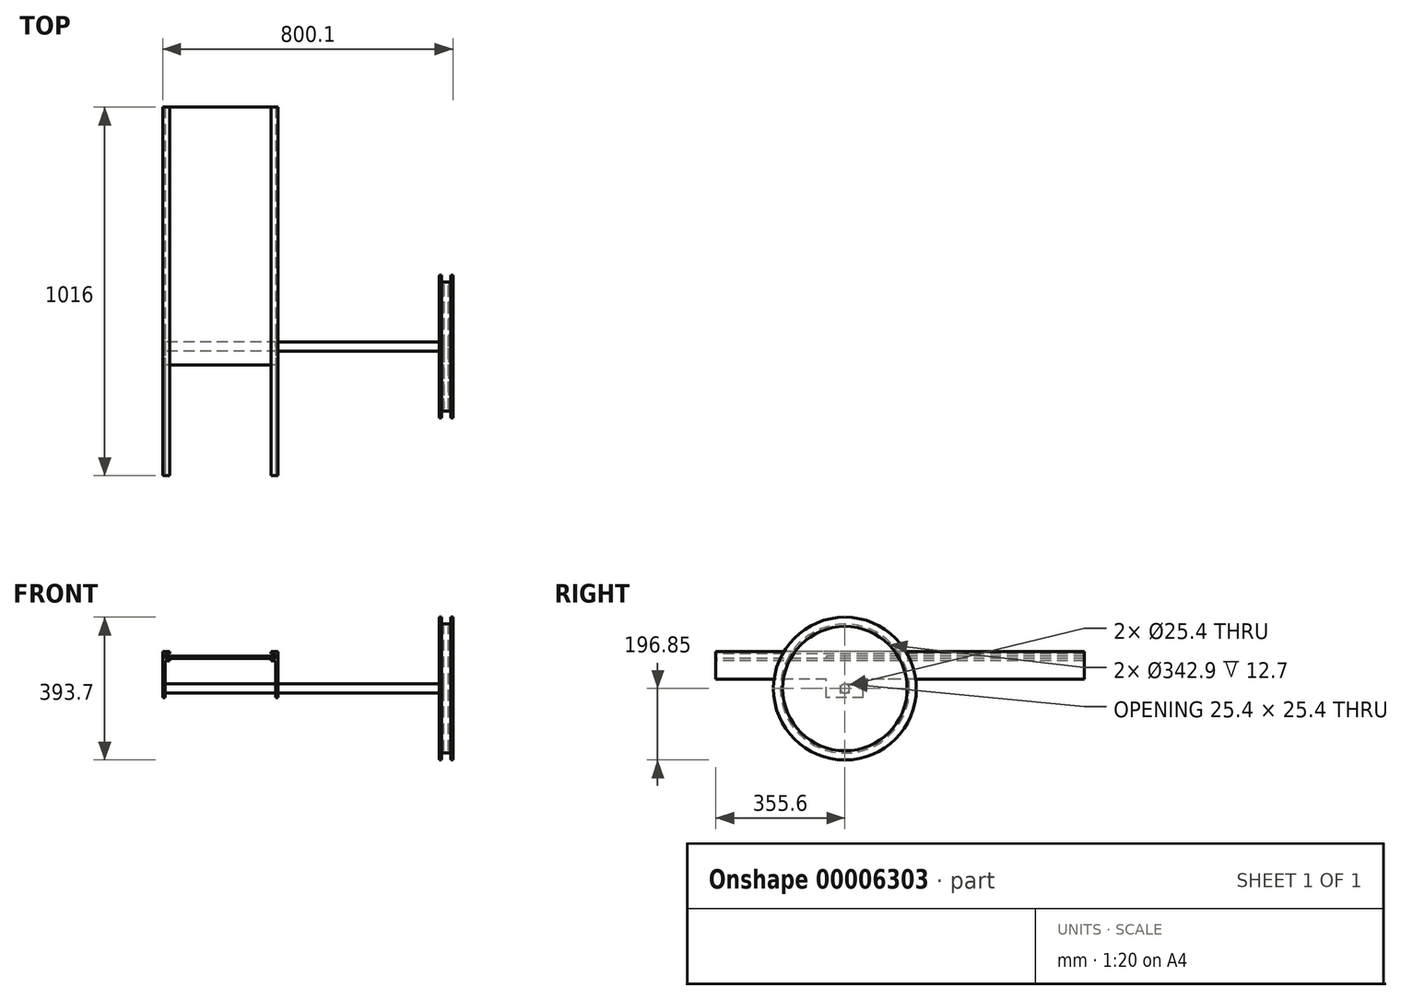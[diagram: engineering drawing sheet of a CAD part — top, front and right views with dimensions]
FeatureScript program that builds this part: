
annotation { "Feature Type Name" : "Feature", "Feature Type Description" : "" }
export const myFeature = defineFeature(function(context is Context, id is Id, definition is map)
    precondition{}
    {
        {
            var Q0;
            Q0=qCreatedBy(makeId("Front.planeOp"),FACE);
            var sketch = newSketch(context, id + "F0", { "sketchPlane" : qUnion([Q0])});
            skLineSegment(sketch, "E0", {"start": v(-158.75, 76.2) * mm, "end": v(-158.75, -50.8) * mm});
            skLineSegment(sketch, "E1", {"start": v(-158.75, -50.8) * mm, "end": v(-152.4, -50.8) * mm});
            skLineSegment(sketch, "E2", {"start": v(-152.4, 50.8) * mm, "end": v(-139.7, 50.8) * mm});
            skLineSegment(sketch, "E3", {"start": v(-139.7, 57.15) * mm, "end": v(-152.4, 57.15) * mm});
            skLineSegment(sketch, "E4", {"start": v(-152.4, 57.15) * mm, "end": v(-152.4, 69.85) * mm});
            skLineSegment(sketch, "E5", {"start": v(-152.4, 69.85) * mm, "end": v(-139.7, 69.85) * mm});
            skLineSegment(sketch, "E6", {"start": v(-139.7, 50.8) * mm, "end": v(-139.7, 57.15) * mm});
            skLineSegment(sketch, "E7", {"start": v(-139.7, 76.2) * mm, "end": v(-158.75, 76.2) * mm});
            skLineSegment(sketch, "E8", {"start": v(-152.4, -50.8) * mm, "end": v(-152.4, 50.8) * mm});
            skLineSegment(sketch, "E9", {"start": v(-152.4, 0) * mm, "end": v(-158.75, 0) * mm});
            skLineSegment(sketch, "E10", {"start": v(-139.7, 76.2) * mm, "end": v(-139.7, 69.85) * mm});
            skLineSegment(sketch, "E11", {"start": v(0, 0) * mm, "end": v(0, 73.55) * mm, "construction": true});
            skLineSegment(sketch, "E12.0.MirrorCS", {"start": v(152.4, -50.8) * mm, "end": v(152.4, 50.8) * mm});
            skLineSegment(sketch, "E12.1.MirrorCS", {"start": v(139.7, 50.8) * mm, "end": v(139.7, 57.15) * mm});
            skLineSegment(sketch, "E12.2.MirrorCS", {"start": v(152.4, 50.8) * mm, "end": v(139.7, 50.8) * mm});
            skLineSegment(sketch, "E12.3.MirrorCS", {"start": v(139.7, 76.2) * mm, "end": v(158.75, 76.2) * mm});
            skLineSegment(sketch, "E12.4.MirrorCS", {"start": v(158.75, -50.8) * mm, "end": v(152.4, -50.8) * mm});
            skLineSegment(sketch, "E12.5.MirrorCS", {"start": v(152.4, 69.85) * mm, "end": v(139.7, 69.85) * mm});
            skLineSegment(sketch, "E12.6.MirrorCS", {"start": v(152.4, 0) * mm, "end": v(158.75, 0) * mm});
            skLineSegment(sketch, "E12.7.MirrorCS", {"start": v(139.7, 57.15) * mm, "end": v(152.4, 57.15) * mm});
            skLineSegment(sketch, "E12.8.MirrorCS", {"start": v(139.7, 76.2) * mm, "end": v(139.7, 69.85) * mm});
            skLineSegment(sketch, "E12.9.MirrorCS", {"start": v(152.4, 57.15) * mm, "end": v(152.4, 69.85) * mm});
            skLineSegment(sketch, "E12.10.MirrorCS", {"start": v(158.75, 76.2) * mm, "end": v(158.75, -50.8) * mm});
            skSolve(sketch);
        }
        {
            var Q0;
            {var subQ2=sQuery(id+"F0.wireOp",EDGE,"E2");Q0=makeQuery(id+"F0.imprint","IMPRINT",FACE,{"disambiguationData":[TD([[makeQuery(id+"F0.imprint","IMPRINT",EDGE,{"derivedFrom":subQ2}),1.0]])]});}
            var Q1;
            Q1=makeQuery(id+"F0.imprint","IMPRINT",FACE,{"disambiguationData":[TD([[makeQuery(id+"F0.imprint","IMPRINT",EDGE,{"derivedFrom":sQuery(id+"F0.wireOp",EDGE,"E12.1.MirrorCS")}),-1.0]])]});
            extrude(context, id + "F1", {"entities" : qUnion([Q0, Q1]), "oppositeDirection" : true, "depth" : 711.2 * mm});
        }
        {
            var Q0;
            Q0=makeQuery(id+"F1.opExtrude","CAP_FACE",FACE,{"disambiguationData":[OSD([sQuery(id+"F0.wireOp",EDGE,"E12.0.MirrorCS"),sQuery(id+"F0.wireOp",EDGE,"E12.1.MirrorCS"),sQuery(id+"F0.wireOp",EDGE,"E12.2.MirrorCS"),sQuery(id+"F0.wireOp",EDGE,"E12.3.MirrorCS"),sQuery(id+"F0.wireOp",EDGE,"E12.5.MirrorCS"),sQuery(id+"F0.wireOp",EDGE,"E12.6.MirrorCS"),sQuery(id+"F0.wireOp",EDGE,"E12.7.MirrorCS"),sQuery(id+"F0.wireOp",EDGE,"E12.8.MirrorCS"),sQuery(id+"F0.wireOp",EDGE,"E12.9.MirrorCS"),sQuery(id+"F0.wireOp",EDGE,"E12.10.MirrorCS")])],"isStart":true});
            var Q1;
            Q1=makeQuery(id+"F1.opExtrude","CAP_FACE",FACE,{"disambiguationData":[OSD([sQuery(id+"F0.wireOp",EDGE,"E0"),sQuery(id+"F0.wireOp",EDGE,"E2"),sQuery(id+"F0.wireOp",EDGE,"E3"),sQuery(id+"F0.wireOp",EDGE,"E4"),sQuery(id+"F0.wireOp",EDGE,"E5"),sQuery(id+"F0.wireOp",EDGE,"E6"),sQuery(id+"F0.wireOp",EDGE,"E7"),sQuery(id+"F0.wireOp",EDGE,"E8"),sQuery(id+"F0.wireOp",EDGE,"E9"),sQuery(id+"F0.wireOp",EDGE,"E10")])],"isStart":true});
            extrude(context, id + "F2", {"entities" : qUnion([Q0, Q1]), "operationType" : NewBodyOperationType.ADD, "depth" : 304.8 * mm});
        }
        {
            var Q0;
            {var subQ2=sQuery(id+"F0.wireOp",EDGE,"E2");Q0=makeQuery(id+"F0.imprint","IMPRINT",FACE,{"disambiguationData":[TD([[makeQuery(id+"F0.imprint","IMPRINT",EDGE,{"derivedFrom":subQ2}),1.0]])]});}
            var Q1;
            {var subQ2=sQuery(id+"F0.wireOp",EDGE,"E1");Q1=makeQuery(id+"F0.imprint","IMPRINT",FACE,{"disambiguationData":[TD([[makeQuery(id+"F0.imprint","IMPRINT",EDGE,{"derivedFrom":subQ2}),1.0]])]});}
            var Q2;
            Q2=makeQuery(id+"F0.imprint","IMPRINT",FACE,{"disambiguationData":[TD([[makeQuery(id+"F0.imprint","IMPRINT",EDGE,{"derivedFrom":sQuery(id+"F0.wireOp",EDGE,"E12.1.MirrorCS")}),-1.0]])]});
            var Q3;
            {var subQ2=sQuery(id+"F0.wireOp",EDGE,"E12.4.MirrorCS");Q3=makeQuery(id+"F0.imprint","IMPRINT",FACE,{"disambiguationData":[TD([[makeQuery(id+"F0.imprint","IMPRINT",EDGE,{"derivedFrom":subQ2}),-1.0]])]});}
            extrude(context, id + "F3", {"entities" : qUnion([Q0, Q1, Q2, Q3]), "operationType" : NewBodyOperationType.ADD, "oppositeDirection" : true, "depth" : 101.6 * mm});
        }
        {
            var Q0;
            {var subQ0=sQuery(id+"F0.wireOp",EDGE,"E0");Q0=makeQuery(id+"F3.boolean.opBoolean","MERGE",FACE,{"derivedFrom":[makeQuery(id+"F2.boolean.opBoolean","MERGE",FACE,{"derivedFrom":[makeQuery(id+"F1.opExtrude","SWEPT_FACE",FACE,{"disambiguationData":[OSD([subQ0])]}),makeQuery(id+"F2.opExtrude","SWEPT_FACE",FACE,{"disambiguationData":[OSD([subQ0])]})]}),makeQuery(id+"F3.opExtrude","SWEPT_FACE",FACE,{"disambiguationData":[OSD([subQ0])]})]});}
            var sketch = newSketch(context, id + "F4", { "sketchPlane" : qUnion([Q0])});
            skLineSegment(sketch, "E13.0", {"start": v(-101.6, 76.2) * mm, "end": v(-101.6, -50.8) * mm});
            skLineSegment(sketch, "E13.1", {"start": v(-101.6, -50.8) * mm, "end": v(0, -50.8) * mm});
            skLineSegment(sketch, "E14.0", {"start": v(0, 76.2) * mm, "end": v(0, -50.8) * mm});
            skCircle(sketch, "E15", {"center": v(-50.8, -25.4) * mm, "radius": 12.7 * mm});
            skLineSegment(sketch, "E16", {"start": v(-50.8, -50.8) * mm, "end": v(-50.8, 76.2) * mm, "construction": true});
            skSolve(sketch);
        }
        {
            var Q0;
            Q0=makeQuery(id+"F4.imprint","IMPRINT",FACE,{"disambiguationData":[TD([[makeQuery(id+"F4.imprint","IMPRINT",EDGE,{"derivedFrom":sQuery(id+"F4.wireOp",EDGE,"E15")}),1.0]])]});
            extrude(context, id + "F5", {"entities" : qUnion([Q0]), "operationType" : NewBodyOperationType.REMOVE, "endBound" : BoundingType.THROUGH_ALL, "oppositeDirection" : true, "depth" : 25.4 * mm});
        }
        {
            var Q0;
            Q0=makeQuery(id+"F4.imprint","IMPRINT",FACE,{"disambiguationData":[TD([[makeQuery(id+"F4.imprint","IMPRINT",EDGE,{"derivedFrom":sQuery(id+"F4.wireOp",EDGE,"E15")}),1.0]])]});
            extrude(context, id + "F6", {"entities" : qUnion([Q0]), "oppositeDirection" : true, "depth" : 787.4 * mm});
        }
        {
            var Q0;
            Q0=qCreatedBy(makeId("Top.planeOp"),FACE);
            var Q1;
            Q1=sQuery(id+"F4.wireOp",VERTEX,"E15.center");
            cPlane(context, id + "F7", {"entities" : qUnion([Q0, Q1]), "cplaneType" : CPlaneType.PLANE_POINT, "offset" : 152.4 * mm, "width" : 152.4 * mm, "height" : 152.4 * mm});
        }
        {
            var Q0;
            Q0=qCreatedBy(id+"F7.planeOp",FACE);
            var sketch = newSketch(context, id + "F8", { "sketchPlane" : qUnion([Q0])});
            skLineSegment(sketch, "E17.0", {"start": v(628.65, 38.1) * mm, "end": v(628.65, 63.5) * mm});
            skLineSegment(sketch, "E18", {"start": v(628.65, 63.5) * mm, "end": v(615.95, 63.5) * mm});
            skLineSegment(sketch, "E19", {"start": v(615.95, 63.5) * mm, "end": v(615.95, 222.25) * mm});
            skLineSegment(sketch, "E20", {"start": v(622.3, 228.6) * mm, "end": v(622.3, 63.5) * mm});
            skLineSegment(sketch, "E21", {"start": v(628.65, 50.8) * mm, "end": v(181.47, 50.8) * mm, "construction": true});
            skLineSegment(sketch, "E22", {"start": v(622.3, 228.6) * mm, "end": v(609.6, 228.6) * mm});
            skLineSegment(sketch, "E23", {"start": v(609.6, 228.6) * mm, "end": v(609.6, 247.65) * mm});
            skLineSegment(sketch, "E24", {"start": v(609.6, 247.65) * mm, "end": v(603.25, 247.65) * mm});
            skLineSegment(sketch, "E25", {"start": v(603.25, 247.65) * mm, "end": v(603.25, 222.25) * mm});
            skLineSegment(sketch, "E26", {"start": v(603.25, 222.25) * mm, "end": v(615.95, 222.25) * mm});
            skLineSegment(sketch, "E27.0.MirrorCS", {"start": v(628.65, 63.5) * mm, "end": v(628.65, 222.25) * mm});
            skLineSegment(sketch, "E28.0.MirrorCS", {"start": v(622.3, 228.6) * mm, "end": v(635, 228.6) * mm});
            skLineSegment(sketch, "E29.0.MirrorCS", {"start": v(635, 228.6) * mm, "end": v(635, 247.65) * mm});
            skLineSegment(sketch, "E30.0.MirrorCS", {"start": v(641.35, 247.65) * mm, "end": v(641.35, 222.25) * mm});
            skLineSegment(sketch, "E31.0.MirrorCS", {"start": v(641.35, 222.25) * mm, "end": v(628.65, 222.25) * mm});
            skLineSegment(sketch, "E32.0.MirrorCS", {"start": v(635, 247.65) * mm, "end": v(641.35, 247.65) * mm});
            skSolve(sketch);
        }
        {
            var Q0;
            {var subQ1=sQuery(id+"F8.wireOp",EDGE,"E20");Q0=makeQuery(id+"F8.imprint","IMPRINT",FACE,{"disambiguationData":[TD([[makeQuery(id+"F8.imprint","IMPRINT",EDGE,{"derivedFrom":subQ1}),1.0]])]});}
            var Q1;
            {var subQ1=sQuery(id+"F8.wireOp",EDGE,"E19");Q1=makeQuery(id+"F8.imprint","IMPRINT",FACE,{"disambiguationData":[TD([[makeQuery(id+"F8.imprint","IMPRINT",EDGE,{"derivedFrom":subQ1}),-1.0]])]});}
            var Q2;
            Q2=sQuery(id+"F8.wireOp",EDGE,"E21");
            revolve(context, id + "F9", {"operationType" : NewBodyOperationType.ADD, "entities" : qUnion([Q0, Q1]), "axis" : qUnion([Q2]), "revolveType" : RevolveType.FULL});
        }
        {
            var Q0;
            {var subQ0=sQuery(id+"F0.wireOp",EDGE,"E12.7.MirrorCS");Q0=makeQuery(id+"F2.boolean.opBoolean","MERGE",FACE,{"derivedFrom":[makeQuery(id+"F1.opExtrude","SWEPT_FACE",FACE,{"disambiguationData":[OSD([subQ0])]}),makeQuery(id+"F2.opExtrude","SWEPT_FACE",FACE,{"disambiguationData":[OSD([subQ0])]})]});}
            var sketch = newSketch(context, id + "F10", { "sketchPlane" : qUnion([Q0])});
            skLineSegment(sketch, "E33.0", {"start": v(152.4, 711.2) * mm, "end": v(152.4, -304.8) * mm});
            skLineSegment(sketch, "E34.0", {"start": v(-152.4, 711.2) * mm, "end": v(-152.4, -304.8) * mm});
            skLineSegment(sketch, "E35.0", {"start": v(152.4, 0) * mm, "end": v(-152.4, 0) * mm});
            skLineSegment(sketch, "E36", {"start": v(-152.4, 711.2) * mm, "end": v(152.4, 711.2) * mm});
            skSolve(sketch);
        }
        {
            var Q0;
            {var subQ5=sQuery(id+"F10.wireOp",EDGE,"E36");var subQ8=sQuery(id+"F10.wireOp",EDGE,"E34.0");var subQ9=makeQuery(id+"F10.imprint","INTERSECT",VERTEX,{"derivedFrom":[subQ8,subQ5]});var subQ11=sQuery(id+"F10.wireOp",EDGE,"E33.0");var subQ12=makeQuery(id+"F10.imprint","INTERSECT",VERTEX,{"derivedFrom":[subQ11,subQ5]});Q0=qUnion([makeQuery(id+"F10.imprint","IMPRINT",FACE,{"disambiguationData":[TD([[makeQuery(id+"F10.imprint","IMPRINT",EDGE,{"disambiguationData":[TD([[subQ9,-1.0]])],"derivedFrom":subQ8}),1.0]])]}),makeQuery(id+"F10.imprint","IMPRINT",FACE,{"disambiguationData":[TD([[makeQuery(id+"F10.imprint","IMPRINT",EDGE,{"disambiguationData":[TD([[subQ12,-1.0]])],"derivedFrom":subQ11}),-1.0]])]})]);}
            extrude(context, id + "F11", {"entities" : qUnion([Q0]), "depth" : 6.35 * mm});
        }
    });
